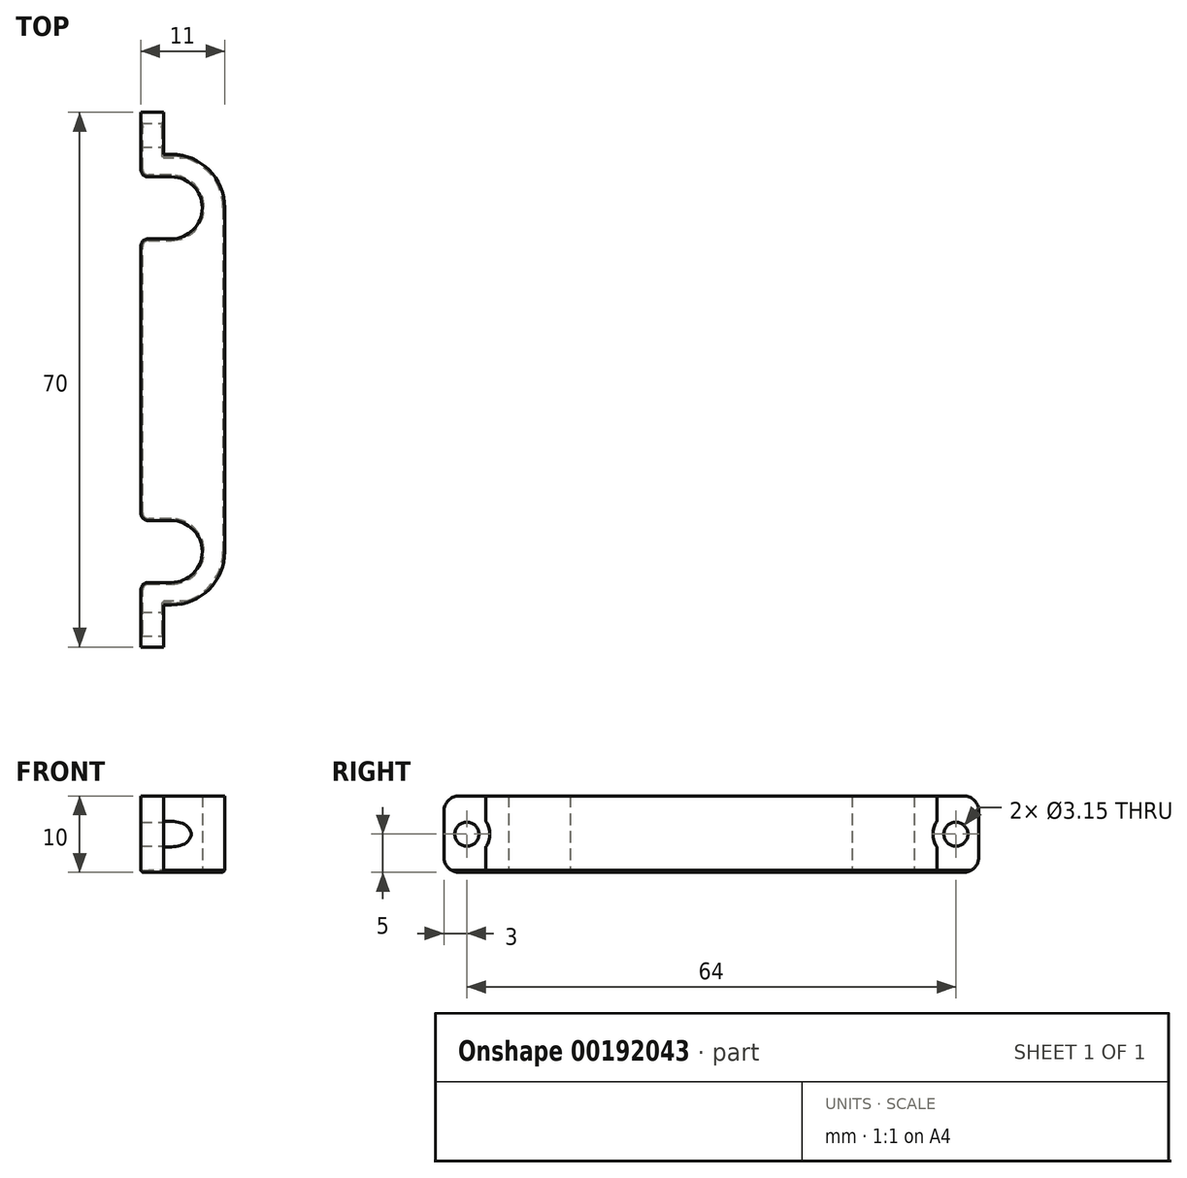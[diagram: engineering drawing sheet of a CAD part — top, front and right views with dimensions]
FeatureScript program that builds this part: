
annotation { "Feature Type Name" : "Feature", "Feature Type Description" : "" }
export const myFeature = defineFeature(function(context is Context, id is Id, definition is map)
    precondition{}
    {
        {
            var Q0;
            Q0=qCreatedBy(makeId("Top.planeOp"),FACE);
            var sketch = newSketch(context, id + "F0", { "sketchPlane" : qUnion([Q0])});
            skCircle(sketch, "E0", {"center": v(0, 22.5) * mm, "radius": 4 * mm, "construction": true});
            skArc(sketch, "E1", {"start": v(0, 26.55) * mm, "mid": v(4.05, 22.5) * mm, "end": v(0, 18.45) * mm});
            skLineSegment(sketch, "E2", {"start": v(0, 18.45) * mm, "end": v(-4, 18.45) * mm});
            skLineSegment(sketch, "E3", {"start": v(-4, 18.45) * mm, "end": v(-4, 0) * mm});
            skLineSegment(sketch, "E4", {"start": v(0, 26.55) * mm, "end": v(-4, 26.55) * mm});
            skLineSegment(sketch, "E5", {"start": v(-4, 26.55) * mm, "end": v(-4, 35) * mm});
            skLineSegment(sketch, "E6", {"start": v(-4, 35) * mm, "end": v(-1, 35) * mm});
            skLineSegment(sketch, "E7", {"start": v(-1, 35) * mm, "end": v(-1, 29.5) * mm});
            skLineSegment(sketch, "E8", {"start": v(-1, 29.5) * mm, "end": v(0, 29.5) * mm});
            skArc(sketch, "E9", {"start": v(0, 29.5) * mm, "mid": v(4.95, 27.45) * mm, "end": v(7, 22.5) * mm});
            skLineSegment(sketch, "E10", {"start": v(7, 22.5) * mm, "end": v(7, 0) * mm});
            skLineSegment(sketch, "E11.MirrorCS", {"start": v(-4, -18.45) * mm, "end": v(-4, 0) * mm});
            skLineSegment(sketch, "E12.MirrorCS", {"start": v(7, -22.5) * mm, "end": v(7, 0) * mm});
            skLineSegment(sketch, "E13.MirrorCS", {"start": v(0, -18.45) * mm, "end": v(-4, -18.45) * mm});
            skArc(sketch, "E14.MirrorCS", {"start": v(0, -26.55) * mm, "mid": v(4.05, -22.5) * mm, "end": v(0, -18.45) * mm});
            skArc(sketch, "E15.MirrorCS", {"start": v(0, -29.5) * mm, "mid": v(4.95, -27.45) * mm, "end": v(7, -22.5) * mm});
            skLineSegment(sketch, "E16.MirrorCS", {"start": v(0, -26.55) * mm, "end": v(-4, -26.55) * mm});
            skLineSegment(sketch, "E17.MirrorCS", {"start": v(-4, -26.55) * mm, "end": v(-4, -35) * mm});
            skCircle(sketch, "E18.MirrorC", {"center": v(0, -22.5) * mm, "radius": 4 * mm, "construction": true});
            skLineSegment(sketch, "E19.MirrorCS", {"start": v(-4, -35) * mm, "end": v(-1, -35) * mm});
            skLineSegment(sketch, "E20.MirrorCS", {"start": v(-1, -35) * mm, "end": v(-1, -29.5) * mm});
            skLineSegment(sketch, "E21.MirrorCS", {"start": v(-1, -29.5) * mm, "end": v(0, -29.5) * mm});
            skPoint(sketch, "E22", {"position": v(-4, 32) * mm});
            skPoint(sketch, "E23.MirrorP", {"position": v(-4, -32) * mm});
            skLineSegment(sketch, "E24", {"start": v(-4, 32) * mm, "end": v(-1, 32) * mm, "construction": true});
            skLineSegment(sketch, "E25.MirrorCS", {"start": v(-4, -32) * mm, "end": v(-1, -32) * mm, "construction": true});
            skSolve(sketch);
        }
        {
            var Q0;
            Q0 = qSketchRegion(id + "F0", true);
            extrude(context, id + "F1", {"entities" : qUnion([Q0]), "depth" : 10 * mm, "symmetric" : true});
        }
        {
            var Q0;
            Q0=makeQuery(id+"F1.opExtrude","SWEPT_EDGE",EDGE,{"disambiguationData":[OSD([sQuery(id+"F0.wireOp",EDGE,"E4"),sQuery(id+"F0.wireOp",EDGE,"E5")])]});
            var Q1;
            Q1=makeQuery(id+"F1.opExtrude","SWEPT_EDGE",EDGE,{"disambiguationData":[OSD([sQuery(id+"F0.wireOp",EDGE,"E2"),sQuery(id+"F0.wireOp",EDGE,"E3")])]});
            var Q2;
            Q2=makeQuery(id+"F1.opExtrude","SWEPT_EDGE",EDGE,{"disambiguationData":[OSD([sQuery(id+"F0.wireOp",EDGE,"E16.MirrorCS"),sQuery(id+"F0.wireOp",EDGE,"E17.MirrorCS")])]});
            var Q3;
            Q3=makeQuery(id+"F1.opExtrude","SWEPT_EDGE",EDGE,{"disambiguationData":[OSD([sQuery(id+"F0.wireOp",EDGE,"E11.MirrorCS"),sQuery(id+"F0.wireOp",EDGE,"E13.MirrorCS")])]});
            fillet(context, id + "F2", {"entities" : qUnion([Q0, Q1, Q2, Q3]), "radius" : 1 * mm, "allowEdgeOverflow" : false});
        }
        {
            var Q0;
            Q0=makeQuery(id+"F1.opExtrude","SWEPT_FACE",FACE,{"disambiguationData":[OSD([sQuery(id+"F0.wireOp",EDGE,"E20.MirrorCS")])]});
            var sketch = newSketch(context, id + "F3", { "sketchPlane" : qUnion([Q0])});
            skPoint(sketch, "E26.0", {"position": v(-32, 0) * mm});
            skCircle(sketch, "E27", {"center": v(-32, 0) * mm, "radius": 1.57 * mm});
            skPoint(sketch, "E28.0", {"position": v(32, 0) * mm});
            skCircle(sketch, "E29", {"center": v(32, 0) * mm, "radius": 1.57 * mm});
            skCircle(sketch, "E30", {"center": v(32, 0) * mm, "radius": 3 * mm});
            skCircle(sketch, "E31", {"center": v(-32, 0) * mm, "radius": 3 * mm});
            skSolve(sketch);
        }
        {
            var Q0;
            Q0=makeQuery(id+"F3.imprint","IMPRINT",FACE,{"disambiguationData":[TD([[makeQuery(id+"F3.imprint","IMPRINT",EDGE,{"derivedFrom":sQuery(id+"F3.wireOp",EDGE,"E29")}),1.0]])]});
            var Q1;
            Q1=makeQuery(id+"F3.imprint","IMPRINT",FACE,{"disambiguationData":[TD([[makeQuery(id+"F3.imprint","IMPRINT",EDGE,{"derivedFrom":sQuery(id+"F3.wireOp",EDGE,"E27")}),1.0]])]});
            var Q2;
            Q2=makeQuery(id+"F1.opExtrude","SWEPT_FACE",FACE,{"disambiguationData":[OSD([sQuery(id+"F0.wireOp",EDGE,"E17.MirrorCS")])]});
            extrude(context, id + "F4", {"entities" : qUnion([Q0, Q1]), "operationType" : NewBodyOperationType.REMOVE, "endBound" : BoundingType.UP_TO_SURFACE, "oppositeDirection" : true, "endBoundEntityFace" : qUnion([Q2]), "depth" : 25 * mm});
        }
        {
            var Q0;
            {var subQ0=sQuery(id+"F3.wireOp",EDGE,"E31");var subQ1=makeQuery(id+"F1.opExtrude","SWEPT_EDGE",EDGE,{"disambiguationData":[OSD([sQuery(id+"F0.wireOp",EDGE,"E20.MirrorCS"),sQuery(id+"F0.wireOp",EDGE,"E21.MirrorCS")])]});var subQ2=makeQuery(id+"F3.imprint","INTERSECT",VERTEX,{"disambiguationData":[OD(0.0)],"derivedFrom":[subQ1,subQ0]});Q0=makeQuery(id+"F3.imprint","IMPRINT",FACE,{"disambiguationData":[TD([[makeQuery(id+"F3.imprint","IMPRINT",EDGE,{"disambiguationData":[TD([[subQ2,1.0]])],"derivedFrom":subQ0}),1.0]])]});}
            var Q1;
            Q1=makeQuery(id+"F3.imprint","IMPRINT",FACE,{"disambiguationData":[TD([[makeQuery(id+"F3.imprint","IMPRINT",EDGE,{"derivedFrom":sQuery(id+"F3.wireOp",EDGE,"E29")}),-1.0]])]});
            extrude(context, id + "F5", {"entities" : qUnion([Q0, Q1]), "operationType" : NewBodyOperationType.REMOVE, "endBound" : BoundingType.THROUGH_ALL, "depth" : 25 * mm});
        }
        {
            var Q0;
            Q0=makeQuery(id+"F1.opExtrude","CAP_EDGE",EDGE,{"disambiguationData":[OSD([sQuery(id+"F0.wireOp",EDGE,"E6")])],"isStart":true});
            var Q1;
            Q1=makeQuery(id+"F1.opExtrude","CAP_EDGE",EDGE,{"disambiguationData":[OSD([sQuery(id+"F0.wireOp",EDGE,"E6")])],"isStart":false});
            var Q2;
            Q2=makeQuery(id+"F1.opExtrude","CAP_EDGE",EDGE,{"disambiguationData":[OSD([sQuery(id+"F0.wireOp",EDGE,"E19.MirrorCS")])],"isStart":true});
            var Q3;
            Q3=makeQuery(id+"F1.opExtrude","CAP_EDGE",EDGE,{"disambiguationData":[OSD([sQuery(id+"F0.wireOp",EDGE,"E19.MirrorCS")])],"isStart":false});
            fillet(context, id + "F6", {"entities" : qUnion([Q0, Q1, Q2, Q3]), "radius" : 2 * mm, "allowEdgeOverflow" : false});
        }
        {
            var Q0;
            Q0=makeQuery(id+"F1.opExtrude","CAP_FACE",FACE,{"disambiguationData":[OSD([sQuery(id+"F0.wireOp",EDGE,"E1"),sQuery(id+"F0.wireOp",EDGE,"E2"),sQuery(id+"F0.wireOp",EDGE,"E3"),sQuery(id+"F0.wireOp",EDGE,"E4"),sQuery(id+"F0.wireOp",EDGE,"E5"),sQuery(id+"F0.wireOp",EDGE,"E6"),sQuery(id+"F0.wireOp",EDGE,"E7"),sQuery(id+"F0.wireOp",EDGE,"E8"),sQuery(id+"F0.wireOp",EDGE,"E9"),sQuery(id+"F0.wireOp",EDGE,"E10"),sQuery(id+"F0.wireOp",EDGE,"E11.MirrorCS"),sQuery(id+"F0.wireOp",EDGE,"E12.MirrorCS"),sQuery(id+"F0.wireOp",EDGE,"E13.MirrorCS"),sQuery(id+"F0.wireOp",EDGE,"E14.MirrorCS"),sQuery(id+"F0.wireOp",EDGE,"E15.MirrorCS"),sQuery(id+"F0.wireOp",EDGE,"E16.MirrorCS"),sQuery(id+"F0.wireOp",EDGE,"E17.MirrorCS"),sQuery(id+"F0.wireOp",EDGE,"E19.MirrorCS"),sQuery(id+"F0.wireOp",EDGE,"E20.MirrorCS"),sQuery(id+"F0.wireOp",EDGE,"E21.MirrorCS")])],"isStart":true});
            chamfer(context, id + "F7", {"entities" : qUnion([Q0]), "width" : 0.25 * mm});
        }
    });
